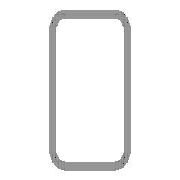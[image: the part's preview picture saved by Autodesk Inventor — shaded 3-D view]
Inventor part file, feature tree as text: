
AUTODESK INVENTOR PART (.ipt)
format: ipt  version: 2025 (Build 290162010, 162A)  size: 150,016 bytes
history: native  units: mm (DEFAULTED — no unit token found)
features: other x4, plane x3, split x2, sketch x1
ambient origin geometry x8: Origin, YZ Plane, XZ Plane, XY Plane, X Axis, Y Axis, Z Axis, Center Point
bodies: Solid1 (feature_tree), Body (feature_tree)
feature tree (10):
  parser-record x1  (decoder bookkeeping rows leaked as tree rows — omitted from the tree; the rows remain in map.json)
  other  "Driven Length"
  other  "Start Plane"
  other  "End Plane"
  plane  "Work Plane4"
  split  "Split1"
  plane  "Work Plane5"
  split  "Split2"
  sketch  "Sketch3"  dims[d3=2180.010215mm d4=0.0mm d7=4.0mm d9=40.0mm d11=80.0mm d12=2.0mm d13=124.457906mm d14=2304.468122mm d15=20.0mm d16=40.0mm d17=90.0deg d18=2180.010215mm]
  plane  "Work Plane3"
